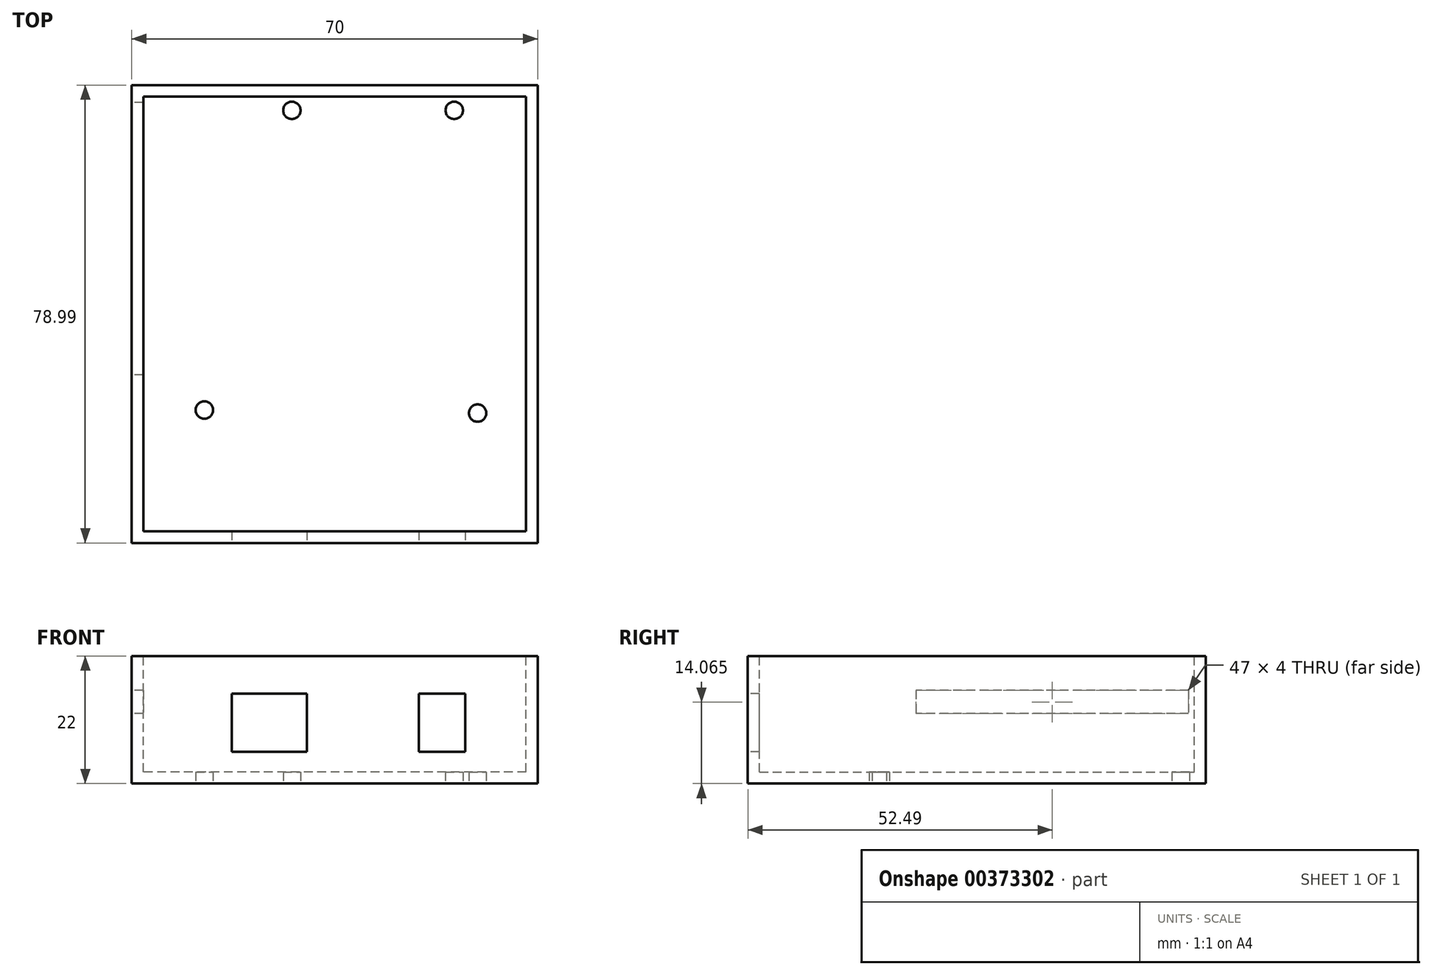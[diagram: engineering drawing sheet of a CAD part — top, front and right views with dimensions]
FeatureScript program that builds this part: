
annotation { "Feature Type Name" : "Feature", "Feature Type Description" : "" }
export const myFeature = defineFeature(function(context is Context, id is Id, definition is map)
    precondition{}
    {
        {
            var Q0;
            Q0=qCreatedBy(makeId("Front.planeOp"),FACE);
            var sketch = newSketch(context, id + "F0", { "sketchPlane" : qUnion([Q0])});
            skLineSegment(sketch, "E0.bottom", {"start": v(35, -11) * mm, "end": v(-35, -11) * mm});
            skLineSegment(sketch, "E0.top", {"start": v(35, 11) * mm, "end": v(-35, 11) * mm});
            skLineSegment(sketch, "E0.left", {"start": v(35, -11) * mm, "end": v(35, 11) * mm});
            skLineSegment(sketch, "E0.right", {"start": v(-35, -11) * mm, "end": v(-35, 11) * mm});
            skPoint(sketch, "E0.middle", {"position": v(0, 0) * mm});
            skSolve(sketch);
        }
        {
            var Q0;
            Q0=makeQuery(id+"F0.imprint","IMPRINT",FACE,{"disambiguationData":[TD([[makeQuery(id+"F0.imprint","IMPRINT",EDGE,{"derivedFrom":sQuery(id+"F0.wireOp",EDGE,"E0.bottom")}),-1.0]])]});
            extrude(context, id + "F1", {"entities" : qUnion([Q0]), "depth" : 79 * mm});
        }
        {
            var Q0;
            Q0=makeQuery(id+"F1.opExtrude","SWEPT_FACE",FACE,{"disambiguationData":[OSD([sQuery(id+"F0.wireOp",EDGE,"E0.top")])]});
            shell(context, id + "F2", {"entities" : qUnion([Q0]), "thickness" : 2 * mm});
        }
        {
            var Q0;
            Q0=makeQuery(id+"F1.opExtrude","CAP_FACE",FACE,{"disambiguationData":[OSD([sQuery(id+"F0.wireOp",EDGE,"E0.bottom"),sQuery(id+"F0.wireOp",EDGE,"E0.top"),sQuery(id+"F0.wireOp",EDGE,"E0.left"),sQuery(id+"F0.wireOp",EDGE,"E0.right")])],"isStart":false});
            var sketch = newSketch(context, id + "F3", { "sketchPlane" : qUnion([Q0])});
            skLineSegment(sketch, "E1.bottom", {"start": v(-17.79, -5.49) * mm, "end": v(-4.79, -5.49) * mm});
            skLineSegment(sketch, "E1.top", {"start": v(-17.79, 4.51) * mm, "end": v(-4.79, 4.51) * mm});
            skLineSegment(sketch, "E1.left", {"start": v(-17.79, -5.49) * mm, "end": v(-17.79, 4.51) * mm});
            skLineSegment(sketch, "E1.right", {"start": v(-4.79, -5.49) * mm, "end": v(-4.79, 4.51) * mm});
            skLineSegment(sketch, "E2.bottom", {"start": v(14.5, -5.5) * mm, "end": v(22.5, -5.5) * mm});
            skLineSegment(sketch, "E2.top", {"start": v(14.5, 4.5) * mm, "end": v(22.5, 4.5) * mm});
            skLineSegment(sketch, "E2.left", {"start": v(14.5, -5.5) * mm, "end": v(14.5, 4.5) * mm});
            skLineSegment(sketch, "E2.right", {"start": v(22.5, -5.5) * mm, "end": v(22.5, 4.5) * mm});
            skSolve(sketch);
        }
        {
            var Q0;
            Q0=makeQuery(id+"F3.imprint","IMPRINT",FACE,{"disambiguationData":[TD([[makeQuery(id+"F3.imprint","IMPRINT",EDGE,{"derivedFrom":sQuery(id+"F3.wireOp",EDGE,"E1.bottom")}),1.0]])]});
            var Q1;
            Q1=makeQuery(id+"F3.imprint","IMPRINT",FACE,{"disambiguationData":[TD([[makeQuery(id+"F3.imprint","IMPRINT",EDGE,{"derivedFrom":sQuery(id+"F3.wireOp",EDGE,"E2.bottom")}),1.0]])]});
            extrude(context, id + "F4", {"entities" : qUnion([Q0, Q1]), "operationType" : NewBodyOperationType.REMOVE, "oppositeDirection" : true, "depth" : 25.4 * mm});
        }
        {
            var Q0;
            Q0=makeQuery(id+"F1.opExtrude","SWEPT_FACE",FACE,{"disambiguationData":[OSD([sQuery(id+"F0.wireOp",EDGE,"E0.right")])]});
            var sketch = newSketch(context, id + "F5", { "sketchPlane" : qUnion([Q0])});
            skLineSegment(sketch, "E3.bottom", {"start": v(3, 5.07) * mm, "end": v(50, 5.07) * mm});
            skLineSegment(sketch, "E3.top", {"start": v(3, 1.07) * mm, "end": v(50, 1.07) * mm});
            skLineSegment(sketch, "E3.left", {"start": v(3, 5.07) * mm, "end": v(3, 1.07) * mm});
            skLineSegment(sketch, "E3.right", {"start": v(50, 5.07) * mm, "end": v(50, 1.07) * mm});
            skSolve(sketch);
        }
        {
            var Q0;
            Q0=makeQuery(id+"F5.imprint","IMPRINT",FACE,{"disambiguationData":[TD([[makeQuery(id+"F5.imprint","IMPRINT",EDGE,{"derivedFrom":sQuery(id+"F5.wireOp",EDGE,"E3.bottom")}),-1.0]])]});
            extrude(context, id + "F6", {"entities" : qUnion([Q0]), "operationType" : NewBodyOperationType.REMOVE, "oppositeDirection" : true, "depth" : 25.4 * mm});
        }
        {
            var Q0;
            Q0=makeQuery(id+"F1.opExtrude","SWEPT_FACE",FACE,{"disambiguationData":[OSD([sQuery(id+"F0.wireOp",EDGE,"E0.bottom")])]});
            var sketch = newSketch(context, id + "F7", { "sketchPlane" : qUnion([Q0])});
            skLineSegment(sketch, "E4", {"start": v(-25.4, 4.35) * mm, "end": v(-7.4, 4.35) * mm});
            skLineSegment(sketch, "E5", {"start": v(-7.4, 4.35) * mm, "end": v(-7.4, 9.35) * mm});
            skPoint(sketch, "E6", {"position": v(-7.4, 4.35) * mm});
            skLineSegment(sketch, "E7", {"start": v(-7.4, 4.35) * mm, "end": v(20.6, 4.35) * mm});
            skPoint(sketch, "E8", {"position": v(20.6, 4.35) * mm});
            skLineSegment(sketch, "E9", {"start": v(22.47, 67.95) * mm, "end": v(22.47, 53.95) * mm});
            skLineSegment(sketch, "E10", {"start": v(25.47, 53.95) * mm, "end": v(22.47, 53.95) * mm});
            skPoint(sketch, "E11", {"position": v(22.47, 53.95) * mm});
            skLineSegment(sketch, "E12", {"start": v(-25.48, 53.05) * mm, "end": v(-22.48, 53.05) * mm});
            skLineSegment(sketch, "E13", {"start": v(-22.48, 68.05) * mm, "end": v(-22.48, 53.05) * mm});
            skPoint(sketch, "E14", {"position": v(-22.48, 53.05) * mm});
            skPoint(sketch, "E15", {"position": v(24.64, 56.57) * mm});
            skLineSegment(sketch, "E16", {"start": v(-22.48, 53.05) * mm, "end": v(-22.48, 56.05) * mm});
            skPoint(sketch, "E17", {"position": v(-22.48, 56.05) * mm});
            skSolve(sketch);
        }
        {
            var Q0;
            Q0=sQuery(id+"F7.wireOp",VERTEX,"E6");
            var Q1;
            Q1=sQuery(id+"F7.wireOp",VERTEX,"E8");
            var Q2;
            Q2=sQuery(id+"F7.wireOp",VERTEX,"E15");
            var Q3;
            Q3=sQuery(id+"F7.wireOp",VERTEX,"E17");
            var Q4;
            Q4=makeQuery(id+"F1.opExtrude","SWEPT_BODY",BODY,{"disambiguationData":[OSD([sQuery(id+"F0.wireOp",EDGE,"E0.bottom"),sQuery(id+"F0.wireOp",EDGE,"E0.top"),sQuery(id+"F0.wireOp",EDGE,"E0.left"),sQuery(id+"F0.wireOp",EDGE,"E0.right")])]});
            hole(context, id + "F8", {"style" : HoleStyle.SIMPLE, "endStyle" : HoleEndStyle.THROUGH, "holeDiameter" : 3 * mm, "isTappedThrough" : true, "tappedDepth" : 12.7 * mm, "tapClearance" : 3, "locations" : qUnion([Q0, Q1, Q2, Q3]), "scope" : qUnion([Q4])});
        }
    });
